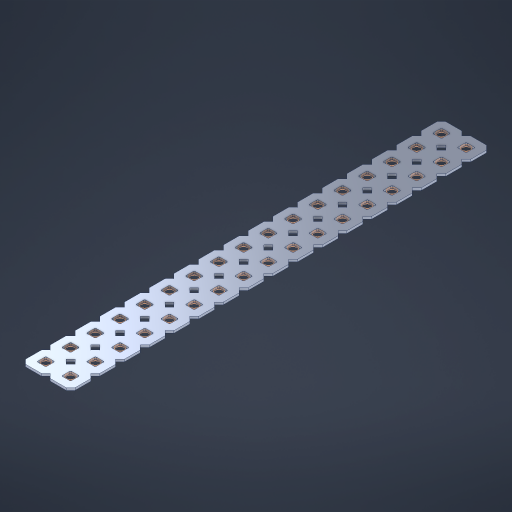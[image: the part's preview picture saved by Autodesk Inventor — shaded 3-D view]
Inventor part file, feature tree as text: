
AUTODESK INVENTOR PART (.ipt)
format: ipt  version: 2023 (Build 270158000, 158)  size: 646,656 bytes
history: native  units: in
note: dims shown in document units (in); Inventor stores cm internally (conversion verified against a paired STEP export)
features: other x35, extrude x33, sketch x2, pattern_linear x1
ambient origin geometry x8: Origin, YZ Plane, XZ Plane, XY Plane, X Axis, Y Axis, Z Axis, Center Point
bodies: Solid1 (feature_tree), Body (feature_tree)
feature tree (71):
  pattern_linear  "Rectangular Pattern1"  Spacing1=0.09in  [1 undecoded]
  sketch  "Sketch1"  dims[d1=0.5in]
  sketch  "Sketch2"  dims[d2=0.182in d3=0.09in d4=0.09in d5=0.09in d6=0.09in d7=0.09in d8=0.09in d9=0.09in d10=0.09in d11=0.02in d13=0.0in d14=0.172in d15=0.0625in d16=0.0in d19=0.5in d22=0.5in]
  other  "Srf1"
  other  "Srf126"
  other  "Srf127"
  other  "Srf128"
  other  "Srf129"
  other  "Srf130"
  other  "Srf131"
  other  "Srf250"
  other  "Srf251"
  other  "Srf252"
  other  "Srf253"
  other  "Srf254"
  other  "Srf255"
  other  "Srf256"
  other  "Srf257"
  other  "Srf258"
  other  "Srf259"
  other  "Srf268"
  other  "Srf269"
  other  "Srf270"
  other  "Srf271"
  other  "Srf272"
  other  "Srf273"
  other  "Srf274"
  other  "Srf275"
  other  "Srf276"
  other  "Srf277"
  other  "Srf278"
  other  "Srf279"
  other  "Srf280"
  other  "Srf281"
  other  "Srf282"
  other  "Srf283"
  other  "Srf284"
  other  "Circle"
  extrude  "ExtrusionSrf126"  Depth=0.09in
  extrude  "ExtrusionSrf127"  Depth=0.09in
  extrude  "ExtrusionSrf128"  Depth=0.09in
  extrude  "ExtrusionSrf129"  Depth=0.09in
  extrude  "ExtrusionSrf130"  Depth=0.09in
  extrude  "ExtrusionSrf131"  Depth=0.09in
  extrude  "ExtrusionSrf250"  Depth=0.09in
  extrude  "ExtrusionSrf251"  Depth=0.02in
  extrude  "ExtrusionSrf252"  TaperAngle=0.0deg  [1 undecoded]
  extrude  "ExtrusionSrf253"  Depth=0.5in
  extrude  "ExtrusionSrf254"  Depth=0.5in TaperAngle=0.0deg
  extrude  "ExtrusionSrf255"  Depth=0.5in
  extrude  "ExtrusionSrf256"  Depth=0.5in
  extrude  "ExtrusionSrf257"  [1 undecoded]
  extrude  "ExtrusionSrf258"  [1 undecoded]
  extrude  "ExtrusionSrf259"  [1 undecoded]
  extrude  "ExtrusionSrf268"  [1 undecoded]
  extrude  "ExtrusionSrf269"  [1 undecoded]
  extrude  "ExtrusionSrf270"  [1 undecoded]
  extrude  "ExtrusionSrf271"  [1 undecoded]
  extrude  "ExtrusionSrf272"  [1 undecoded]
  extrude  "ExtrusionSrf273"  [1 undecoded]
  extrude  "ExtrusionSrf274"  [1 undecoded]
  extrude  "ExtrusionSrf275"  [1 undecoded]
  extrude  "ExtrusionSrf276"  [1 undecoded]
  extrude  "ExtrusionSrf277"  [1 undecoded]
  extrude  "ExtrusionSrf278"  [1 undecoded]
  extrude  "ExtrusionSrf279"  [1 undecoded]
  extrude  "ExtrusionSrf280"  [1 undecoded]
  extrude  "ExtrusionSrf281"  [1 undecoded]
  extrude  "ExtrusionSrf282"  [1 undecoded]
  extrude  "ExtrusionSrf283"  [1 undecoded]
  extrude  "ExtrusionSrf284"  [1 undecoded]
note: 22 required parameter values undecoded (feature->parameter linkage not recoverable at this tier; creation-order binding heuristic only, values carry confidence <= 0.55)
